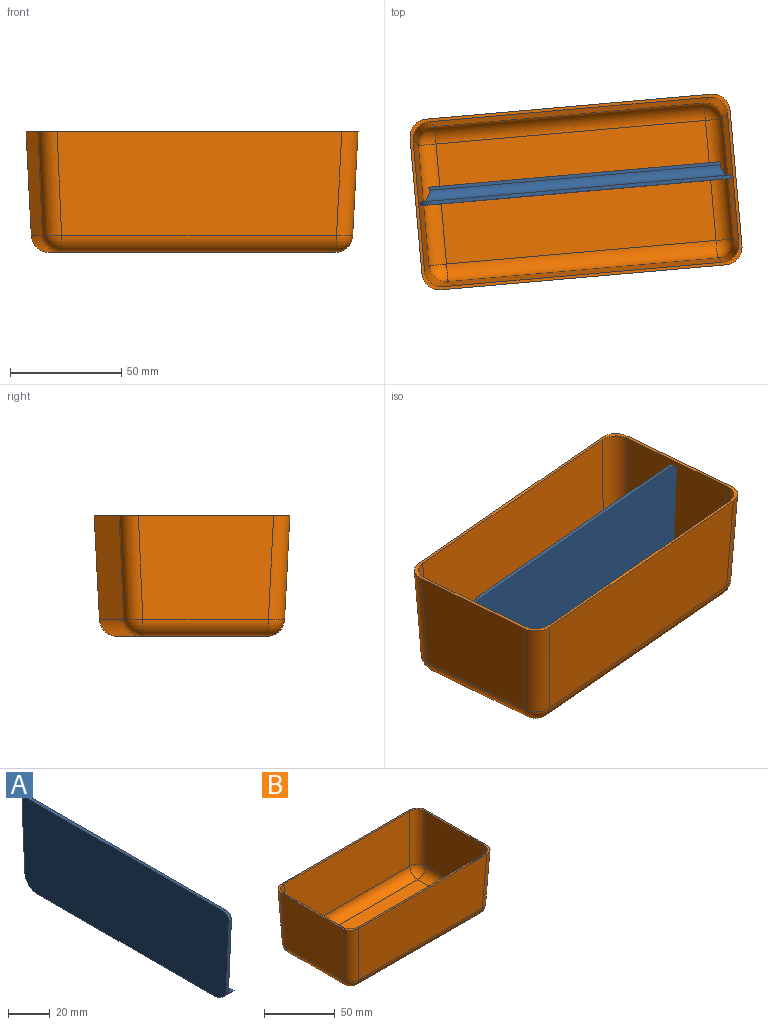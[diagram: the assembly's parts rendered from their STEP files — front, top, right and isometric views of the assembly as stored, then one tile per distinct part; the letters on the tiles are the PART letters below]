
ASSEMBLY  parts=2 mates=1
PART A: 13 faces, bbox 8x140.8x53 mm
  f0: plane 120.94x8mm, normal (0,0,-1), area 967.5mm2, adj f1,f5,f8,f9
  f1: plane 131.52x2mm, normal (1,0,0), area 256.4mm2, adj f0,f2,f8,f9
  f2: plane 131.52x1.4mm, normal (0,0,1), area 184.1mm2, adj f1,f8,f9,f10
  f3: plane 140.81x46mm, normal (1,0,0), area 6387.7mm2, adj f4,f6,f7,f8,f9,f10,f11,f12
  f4: plane 132.81x1.6mm, normal (0,0,1), area 212.5mm2, adj f3,f5,f11,f12
  f5: plane 140.81x53mm, normal (-1,0,0), area 7318.9mm2, adj f0,f4,f6,f7,f8,f9,f11,f12
  f6: plane 41.19x1.94mm, normal (0,-1,-0.05), area 66mm2, adj f3,f5,f9,f12
  f7: plane 41.19x1.94mm, normal (0,1,-0.05), area 66mm2, adj f3,f5,f8,f11
  f8: cylinder r=8mm len=8mm, axis (1,0,0), area 63.5mm2, adj f0,f1,f2,f3,f5,f7,f10
  f9: cylinder r=8mm len=8mm, axis (1,0,0), area 63.5mm2, adj f0,f1,f2,f3,f5,f6,f10
  f10: cylinder r=5mm len=136.81mm, axis (0,1,0), area 1053.2mm2, adj f2,f3,f8,f9
  f11: cylinder r=4mm len=4.19mm, axis (-1,0,0), area 10.4mm2, adj f3,f4,f5,f7
  f12: cylinder r=4mm len=4.19mm, axis (-1,0,0), area 10.4mm2, adj f3,f4,f5,f6
PART B: 35 faces, bbox 144.6x77.1x54.5 mm
  f0: plane 61.12x46.68mm, normal (1,0,-0.05), area 2753.1mm2, adj f8,f13,f16,f26
  f1: plane 128.62x46.68mm, normal (0,1,-0.05), area 5907.3mm2, adj f8,f13,f14,f22
  f2: plane 61.12x46.68mm, normal (-1,0,-0.05), area 2753.1mm2, adj f8,f14,f15,f19
  f3: plane 58.52x45.38mm, normal (1,0,0.05), area 2561.1mm2, adj f8,f9,f12,f32
  f4: plane 126.02x45.38mm, normal (0,-1,0.05), area 5627.4mm2, adj f8,f9,f10,f28
  f5: plane 58.52x45.38mm, normal (-1,0,0.05), area 2561.1mm2, adj f8,f10,f11,f29
  f6: plane 126.02x45.38mm, normal (0,1,0.05), area 5627.4mm2, adj f8,f11,f12,f33
  f7: plane 128.62x46.68mm, normal (0,-1,-0.05), area 5907.3mm2, adj f8,f15,f16,f23
  f8: plane 144.6x77.1mm, normal (0,0,1), area 569.7mm2, adj f0,f1,f2,f3,f4,f5,f6,f7
  f9: cylinder r=8mm len=45.69mm, axis (0.05,-0.05,-1), area 572mm2, adj f3,f4,f8,f30
  f10: cylinder r=8mm len=45.69mm, axis (-0.05,-0.05,-1), area 572mm2, adj f4,f5,f8,f27
  f11: cylinder r=8mm len=45.69mm, axis (-0.05,0.05,-1), area 572mm2, adj f5,f6,f8,f31
  f12: cylinder r=8mm len=45.69mm, axis (0.05,0.05,-1), area 572mm2, adj f3,f6,f8,f34
  f13: cylinder r=8mm len=46.99mm, axis (0.05,0.05,1), area 588.3mm2, adj f0,f1,f8,f24
  f14: cylinder r=8mm len=46.99mm, axis (-0.05,0.05,1), area 588.3mm2, adj f1,f2,f8,f20
  f15: cylinder r=8mm len=46.99mm, axis (-0.05,-0.05,1), area 588.3mm2, adj f2,f7,f8,f21
  f16: cylinder r=8mm len=46.99mm, axis (0.05,-0.05,1), area 588.3mm2, adj f0,f7,f8,f25
  f17: plane 121.74x54.24mm, normal (0,0,1), area 6602.8mm2, adj f28,f29,f32,f33
  f18: plane 124.22x56.72mm, normal (0,0,-1), area 7044.9mm2, adj f19,f22,f23,f26
  f19: cylinder r=8mm len=56.72mm, axis (0,1,0), area 691.3mm2, adj f2,f18,f20,f21
  f20: sphere r=8mm, area 94.5mm2, adj f14,f19,f22
  f21: sphere r=8mm, area 94.5mm2, adj f15,f19,f23
  f22: cylinder r=8mm len=124.22mm, axis (1,0,0), area 1514.1mm2, adj f1,f18,f20,f24
  f23: cylinder r=8mm len=124.22mm, axis (1,0,0), area 1514.1mm2, adj f7,f18,f21,f25
  f24: sphere r=8mm, area 94.5mm2, adj f13,f22,f26
  f25: sphere r=8mm, area 94.5mm2, adj f16,f23,f26
  f26: cylinder r=8mm len=56.72mm, axis (0,-1,0), area 691.3mm2, adj f0,f18,f24,f25
  f27: sphere r=8mm, area 94.5mm2, adj f10,f28,f29
  f28: cylinder r=8mm len=121.74mm, axis (-1,0,0), area 1483.9mm2, adj f4,f17,f27,f30
  f29: cylinder r=8mm len=54.24mm, axis (0,-1,0), area 661.1mm2, adj f5,f17,f27,f31
  f30: sphere r=8mm, area 94.5mm2, adj f9,f28,f32
  f31: sphere r=8mm, area 94.5mm2, adj f11,f29,f33
  f32: cylinder r=8mm len=54.24mm, axis (0,-1,0), area 661.1mm2, adj f3,f17,f30,f34
  f33: cylinder r=8mm len=121.74mm, axis (-1,0,0), area 1483.9mm2, adj f6,f17,f31,f34
  f34: sphere r=8mm, area 94.5mm2, adj f12,f32,f33
PLACE A rot(axis=(0,0,1),95deg) t=(-0.85,4.73,-15.91)mm
PLACE B rot(axis=(0,0,1),5deg) t=(-0.85,4.73,-15.91)mm
MATE revolute A.f0 <-> B.f17  axis (0,0,1) through (-0.85,4.73,-15.91)mm
